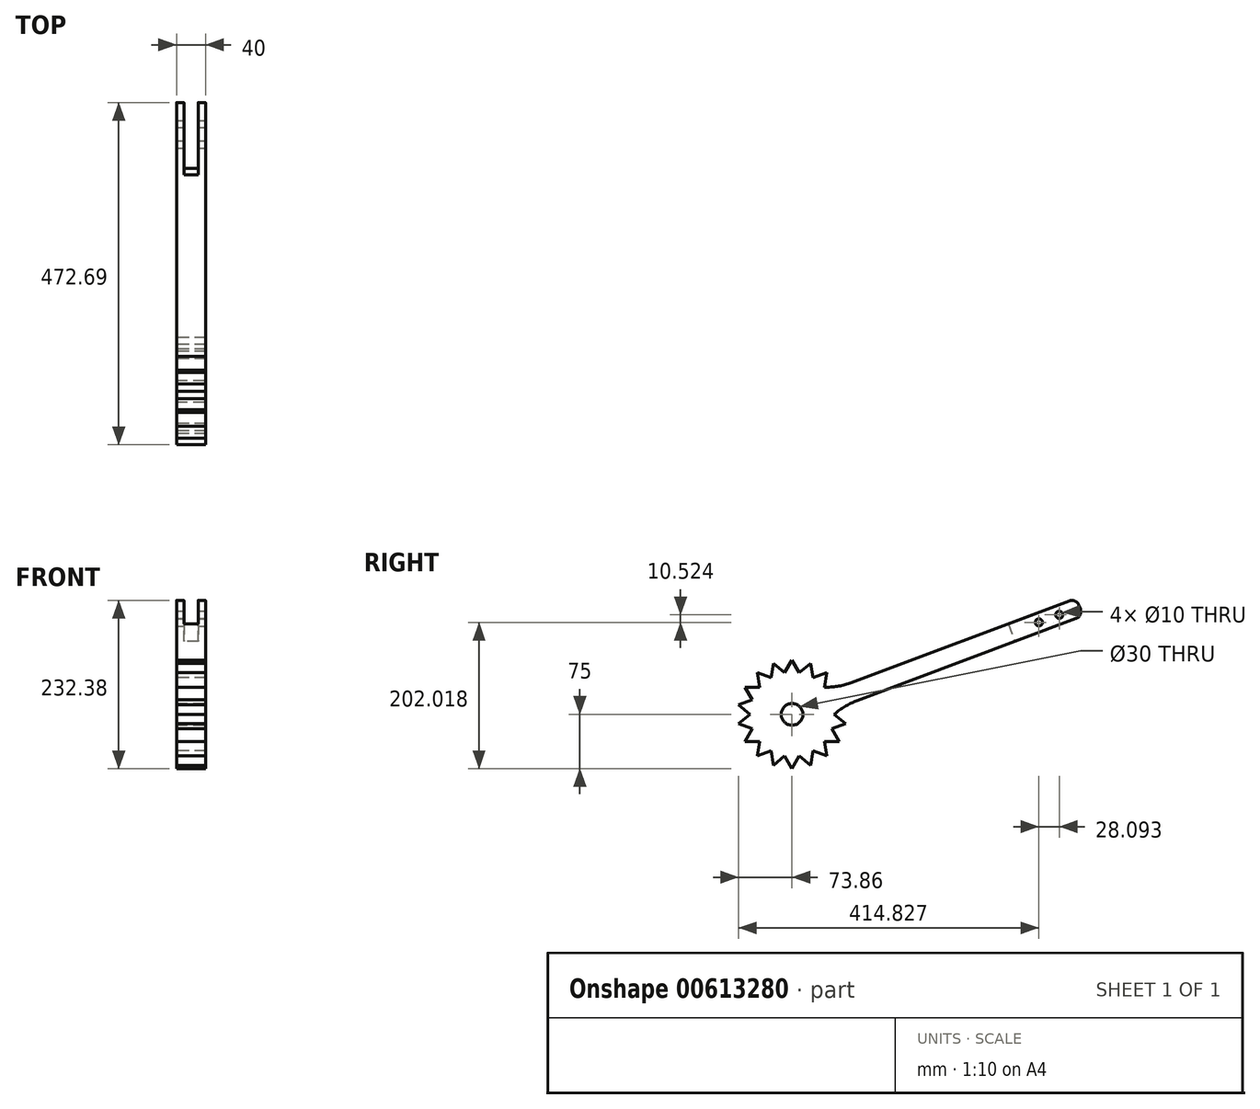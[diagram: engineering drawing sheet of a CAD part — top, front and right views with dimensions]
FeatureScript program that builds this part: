
annotation { "Feature Type Name" : "Feature", "Feature Type Description" : "" }
export const myFeature = defineFeature(function(context is Context, id is Id, definition is map)
    precondition{}
    {
        {
            var Q0;
            Q0=qCreatedBy(makeId("Right.planeOp"),FACE);
            var sketch = newSketch(context, id + "F0", { "sketchPlane" : qUnion([Q0])});
            skCircle(sketch, "E0", {"center": v(0, 0) * mm, "radius": 15 * mm});
            skCircle(sketch, "E1", {"center": v(0, 0) * mm, "radius": 37.5 * mm});
            skCircle(sketch, "E2.cCircle", {"center": v(0, 0) * mm, "radius": 37.5 * mm, "construction": true});
            skLineSegment(sketch, "E2.0", {"start": v(-64.95, 37.5) * mm, "end": v(64.95, 37.5) * mm});
            skLineSegment(sketch, "E2.1", {"start": v(64.95, 37.5) * mm, "end": v(0, -75) * mm});
            skLineSegment(sketch, "E2.2", {"start": v(0, -75) * mm, "end": v(-64.95, 37.5) * mm});
            skPoint(sketch, "E2.0.midPoint", {"position": v(0, 37.5) * mm});
            skLineSegment(sketch, "E3.0", {"start": v(-25.65, 70.48) * mm, "end": v(73.86, -13.02) * mm});
            skLineSegment(sketch, "E3.1", {"start": v(73.86, -13.02) * mm, "end": v(-48.2, -57.45) * mm});
            skLineSegment(sketch, "E3.2", {"start": v(-48.2, -57.45) * mm, "end": v(-25.65, 70.48) * mm});
            skPoint(sketch, "E3.0.midPoint", {"position": v(24.1, 28.73) * mm});
            skLineSegment(sketch, "E4.0", {"start": v(48.2, -57.45) * mm, "end": v(-73.86, -13.02) * mm});
            skLineSegment(sketch, "E4.1", {"start": v(-73.86, -13.02) * mm, "end": v(25.65, 70.48) * mm});
            skLineSegment(sketch, "E4.2", {"start": v(25.65, 70.48) * mm, "end": v(48.2, -57.45) * mm});
            skPoint(sketch, "E4.0.midPoint", {"position": v(-12.83, -35.24) * mm});
            skLineSegment(sketch, "E5.0", {"start": v(64.95, -37.5) * mm, "end": v(-64.95, -37.5) * mm});
            skLineSegment(sketch, "E5.1", {"start": v(-64.95, -37.5) * mm, "end": v(0, 75) * mm});
            skLineSegment(sketch, "E5.2", {"start": v(0, 75) * mm, "end": v(64.95, -37.5) * mm});
            skPoint(sketch, "E5.0.midPoint", {"position": v(0, -37.5) * mm});
            skLineSegment(sketch, "E6.0", {"start": v(25.65, -70.48) * mm, "end": v(-73.86, 13.02) * mm});
            skLineSegment(sketch, "E6.1", {"start": v(-73.86, 13.02) * mm, "end": v(48.2, 57.45) * mm});
            skLineSegment(sketch, "E6.2", {"start": v(48.2, 57.45) * mm, "end": v(25.65, -70.48) * mm});
            skPoint(sketch, "E6.0.midPoint", {"position": v(-24.1, -28.73) * mm});
            skLineSegment(sketch, "E7.0", {"start": v(73.86, 13.02) * mm, "end": v(-25.65, -70.48) * mm});
            skLineSegment(sketch, "E7.1", {"start": v(-25.65, -70.48) * mm, "end": v(-48.2, 57.45) * mm});
            skLineSegment(sketch, "E7.2", {"start": v(-48.2, 57.45) * mm, "end": v(73.86, 13.02) * mm});
            skPoint(sketch, "E7.0.midPoint", {"position": v(24.1, -28.73) * mm});
            skSolve(sketch);
        }
        {
            var Q0;
            {var subQ0=sQuery(id+"F0.wireOp",EDGE,"E2.2");var subQ1=sQuery(id+"F0.wireOp",EDGE,"E2.0");var subQ2=makeQuery(id+"F0.imprint","INTERSECT",VERTEX,{"derivedFrom":[subQ1,subQ0]});Q0=makeQuery(id+"F0.imprint","IMPRINT",FACE,{"disambiguationData":[TD([[makeQuery(id+"F0.imprint","IMPRINT",EDGE,{"disambiguationData":[TD([[subQ2,-1.0]])],"derivedFrom":subQ1}),-1.0]])]});}
            var Q1;
            {var subQ0=sQuery(id+"F0.wireOp",EDGE,"E7.1");var subQ1=sQuery(id+"F0.wireOp",EDGE,"E2.0");var subQ2=makeQuery(id+"F0.imprint","INTERSECT",VERTEX,{"derivedFrom":[subQ1,subQ0]});Q1=makeQuery(id+"F0.imprint","IMPRINT",FACE,{"disambiguationData":[TD([[makeQuery(id+"F0.imprint","IMPRINT",EDGE,{"disambiguationData":[TD([[subQ2,-1.0]])],"derivedFrom":subQ1}),1.0]])]});}
            var Q2;
            {var subQ0=sQuery(id+"F0.wireOp",EDGE,"E6.2");var subQ1=sQuery(id+"F0.wireOp",EDGE,"E2.0");var subQ2=makeQuery(id+"F0.imprint","INTERSECT",VERTEX,{"derivedFrom":[subQ1,subQ0]});Q2=makeQuery(id+"F0.imprint","IMPRINT",FACE,{"disambiguationData":[TD([[makeQuery(id+"F0.imprint","IMPRINT",EDGE,{"disambiguationData":[TD([[subQ2,1.0]])],"derivedFrom":subQ1}),1.0]])]});}
            var Q3;
            {var subQ0=sQuery(id+"F0.wireOp",EDGE,"E2.1");var subQ1=sQuery(id+"F0.wireOp",EDGE,"E2.0");var subQ2=makeQuery(id+"F0.imprint","INTERSECT",VERTEX,{"derivedFrom":[subQ1,subQ0]});Q3=makeQuery(id+"F0.imprint","IMPRINT",FACE,{"disambiguationData":[TD([[makeQuery(id+"F0.imprint","IMPRINT",EDGE,{"disambiguationData":[TD([[subQ2,1.0]])],"derivedFrom":subQ1}),-1.0]])]});}
            var Q4;
            {var subQ0=sQuery(id+"F0.wireOp",EDGE,"E7.2");var subQ1=sQuery(id+"F0.wireOp",EDGE,"E2.1");var subQ2=makeQuery(id+"F0.imprint","INTERSECT",VERTEX,{"derivedFrom":[subQ1,subQ0]});Q4=makeQuery(id+"F0.imprint","IMPRINT",FACE,{"disambiguationData":[TD([[makeQuery(id+"F0.imprint","IMPRINT",EDGE,{"disambiguationData":[TD([[subQ2,-1.0]])],"derivedFrom":subQ1}),1.0]])]});}
            var Q5;
            {var subQ0=sQuery(id+"F0.wireOp",EDGE,"E6.0");var subQ1=sQuery(id+"F0.wireOp",EDGE,"E2.1");var subQ2=makeQuery(id+"F0.imprint","INTERSECT",VERTEX,{"derivedFrom":[subQ1,subQ0]});Q5=makeQuery(id+"F0.imprint","IMPRINT",FACE,{"disambiguationData":[TD([[makeQuery(id+"F0.imprint","IMPRINT",EDGE,{"disambiguationData":[TD([[subQ2,1.0]])],"derivedFrom":subQ1}),1.0]])]});}
            var Q6;
            {var subQ0=sQuery(id+"F0.wireOp",EDGE,"E2.2");var subQ1=sQuery(id+"F0.wireOp",EDGE,"E2.1");var subQ2=makeQuery(id+"F0.imprint","INTERSECT",VERTEX,{"derivedFrom":[subQ1,subQ0]});Q6=makeQuery(id+"F0.imprint","IMPRINT",FACE,{"disambiguationData":[TD([[makeQuery(id+"F0.imprint","IMPRINT",EDGE,{"disambiguationData":[TD([[subQ2,1.0]])],"derivedFrom":subQ1}),-1.0]])]});}
            var Q7;
            {var subQ0=sQuery(id+"F0.wireOp",EDGE,"E7.0");var subQ1=sQuery(id+"F0.wireOp",EDGE,"E2.2");var subQ2=makeQuery(id+"F0.imprint","INTERSECT",VERTEX,{"derivedFrom":[subQ1,subQ0]});Q7=makeQuery(id+"F0.imprint","IMPRINT",FACE,{"disambiguationData":[TD([[makeQuery(id+"F0.imprint","IMPRINT",EDGE,{"disambiguationData":[TD([[subQ2,-1.0]])],"derivedFrom":subQ1}),1.0]])]});}
            var Q8;
            {var subQ0=sQuery(id+"F0.wireOp",EDGE,"E6.1");var subQ1=sQuery(id+"F0.wireOp",EDGE,"E2.2");var subQ2=makeQuery(id+"F0.imprint","INTERSECT",VERTEX,{"derivedFrom":[subQ1,subQ0]});Q8=makeQuery(id+"F0.imprint","IMPRINT",FACE,{"disambiguationData":[TD([[makeQuery(id+"F0.imprint","IMPRINT",EDGE,{"disambiguationData":[TD([[subQ2,1.0]])],"derivedFrom":subQ1}),1.0]])]});}
            var Q9;
            {var subQ0=sQuery(id+"F0.wireOp",EDGE,"E3.2");var subQ1=sQuery(id+"F0.wireOp",EDGE,"E3.0");var subQ2=makeQuery(id+"F0.imprint","INTERSECT",VERTEX,{"derivedFrom":[subQ1,subQ0]});Q9=makeQuery(id+"F0.imprint","IMPRINT",FACE,{"disambiguationData":[TD([[makeQuery(id+"F0.imprint","IMPRINT",EDGE,{"disambiguationData":[TD([[subQ2,-1.0]])],"derivedFrom":subQ1}),-1.0]])]});}
            var Q10;
            {var subQ0=sQuery(id+"F0.wireOp",EDGE,"E5.1");var subQ1=sQuery(id+"F0.wireOp",EDGE,"E3.0");var subQ2=makeQuery(id+"F0.imprint","INTERSECT",VERTEX,{"derivedFrom":[subQ1,subQ0]});Q10=makeQuery(id+"F0.imprint","IMPRINT",FACE,{"disambiguationData":[TD([[makeQuery(id+"F0.imprint","IMPRINT",EDGE,{"disambiguationData":[TD([[subQ2,-1.0]])],"derivedFrom":subQ1}),1.0]])]});}
            var Q11;
            {var subQ0=sQuery(id+"F0.wireOp",EDGE,"E3.1");var subQ1=sQuery(id+"F0.wireOp",EDGE,"E3.0");var subQ2=makeQuery(id+"F0.imprint","INTERSECT",VERTEX,{"derivedFrom":[subQ1,subQ0]});Q11=makeQuery(id+"F0.imprint","IMPRINT",FACE,{"disambiguationData":[TD([[makeQuery(id+"F0.imprint","IMPRINT",EDGE,{"disambiguationData":[TD([[subQ2,1.0]])],"derivedFrom":subQ1}),-1.0]])]});}
            var Q12;
            {var subQ0=sQuery(id+"F0.wireOp",EDGE,"E5.2");var subQ1=sQuery(id+"F0.wireOp",EDGE,"E3.1");var subQ2=makeQuery(id+"F0.imprint","INTERSECT",VERTEX,{"derivedFrom":[subQ1,subQ0]});Q12=makeQuery(id+"F0.imprint","IMPRINT",FACE,{"disambiguationData":[TD([[makeQuery(id+"F0.imprint","IMPRINT",EDGE,{"disambiguationData":[TD([[subQ2,-1.0]])],"derivedFrom":subQ1}),1.0]])]});}
            var Q13;
            {var subQ0=sQuery(id+"F0.wireOp",EDGE,"E3.2");var subQ1=sQuery(id+"F0.wireOp",EDGE,"E3.1");var subQ2=makeQuery(id+"F0.imprint","INTERSECT",VERTEX,{"derivedFrom":[subQ1,subQ0]});Q13=makeQuery(id+"F0.imprint","IMPRINT",FACE,{"disambiguationData":[TD([[makeQuery(id+"F0.imprint","IMPRINT",EDGE,{"disambiguationData":[TD([[subQ2,1.0]])],"derivedFrom":subQ1}),-1.0]])]});}
            var Q14;
            {var subQ0=sQuery(id+"F0.wireOp",EDGE,"E5.0");var subQ1=sQuery(id+"F0.wireOp",EDGE,"E3.2");var subQ2=makeQuery(id+"F0.imprint","INTERSECT",VERTEX,{"derivedFrom":[subQ1,subQ0]});Q14=makeQuery(id+"F0.imprint","IMPRINT",FACE,{"disambiguationData":[TD([[makeQuery(id+"F0.imprint","IMPRINT",EDGE,{"disambiguationData":[TD([[subQ2,-1.0]])],"derivedFrom":subQ1}),1.0]])]});}
            var Q15;
            {var subQ0=sQuery(id+"F0.wireOp",EDGE,"E4.2");var subQ1=sQuery(id+"F0.wireOp",EDGE,"E4.0");var subQ2=makeQuery(id+"F0.imprint","INTERSECT",VERTEX,{"derivedFrom":[subQ1,subQ0]});Q15=makeQuery(id+"F0.imprint","IMPRINT",FACE,{"disambiguationData":[TD([[makeQuery(id+"F0.imprint","IMPRINT",EDGE,{"disambiguationData":[TD([[subQ2,-1.0]])],"derivedFrom":subQ1}),-1.0]])]});}
            var Q16;
            {var subQ0=sQuery(id+"F0.wireOp",EDGE,"E4.1");var subQ1=sQuery(id+"F0.wireOp",EDGE,"E4.0");var subQ2=makeQuery(id+"F0.imprint","INTERSECT",VERTEX,{"derivedFrom":[subQ1,subQ0]});Q16=makeQuery(id+"F0.imprint","IMPRINT",FACE,{"disambiguationData":[TD([[makeQuery(id+"F0.imprint","IMPRINT",EDGE,{"disambiguationData":[TD([[subQ2,1.0]])],"derivedFrom":subQ1}),-1.0]])]});}
            var Q17;
            {var subQ0=sQuery(id+"F0.wireOp",EDGE,"E4.2");var subQ1=sQuery(id+"F0.wireOp",EDGE,"E4.1");var subQ2=makeQuery(id+"F0.imprint","INTERSECT",VERTEX,{"derivedFrom":[subQ1,subQ0]});Q17=makeQuery(id+"F0.imprint","IMPRINT",FACE,{"disambiguationData":[TD([[makeQuery(id+"F0.imprint","IMPRINT",EDGE,{"disambiguationData":[TD([[subQ2,1.0]])],"derivedFrom":subQ1}),-1.0]])]});}
            var Q18;
            {var subQ0=sQuery(id+"F0.wireOp",EDGE,"E7.1");var subQ1=sQuery(id+"F0.wireOp",EDGE,"E2.0");var subQ2=makeQuery(id+"F0.imprint","INTERSECT",VERTEX,{"derivedFrom":[subQ1,subQ0]});Q18=makeQuery(id+"F0.imprint","IMPRINT",FACE,{"disambiguationData":[TD([[makeQuery(id+"F0.imprint","IMPRINT",EDGE,{"disambiguationData":[TD([[subQ2,-1.0]])],"derivedFrom":subQ1}),-1.0]])]});}
            var Q19;
            {var subQ0=sQuery(id+"F0.wireOp",EDGE,"E3.2");var subQ1=sQuery(id+"F0.wireOp",EDGE,"E2.0");var subQ2=makeQuery(id+"F0.imprint","INTERSECT",VERTEX,{"derivedFrom":[subQ1,subQ0]});Q19=makeQuery(id+"F0.imprint","IMPRINT",FACE,{"disambiguationData":[TD([[makeQuery(id+"F0.imprint","IMPRINT",EDGE,{"disambiguationData":[TD([[subQ2,-1.0]])],"derivedFrom":subQ1}),1.0]])]});}
            var Q20;
            {var subQ0=sQuery(id+"F0.wireOp",EDGE,"E5.2");var subQ1=sQuery(id+"F0.wireOp",EDGE,"E2.0");var subQ2=makeQuery(id+"F0.imprint","INTERSECT",VERTEX,{"derivedFrom":[subQ1,subQ0]});Q20=makeQuery(id+"F0.imprint","IMPRINT",FACE,{"disambiguationData":[TD([[makeQuery(id+"F0.imprint","IMPRINT",EDGE,{"disambiguationData":[TD([[subQ2,-1.0]])],"derivedFrom":subQ1}),1.0]])]});}
            var Q21;
            {var subQ0=sQuery(id+"F0.wireOp",EDGE,"E6.2");var subQ1=sQuery(id+"F0.wireOp",EDGE,"E2.0");var subQ2=makeQuery(id+"F0.imprint","INTERSECT",VERTEX,{"derivedFrom":[subQ1,subQ0]});Q21=makeQuery(id+"F0.imprint","IMPRINT",FACE,{"disambiguationData":[TD([[makeQuery(id+"F0.imprint","IMPRINT",EDGE,{"disambiguationData":[TD([[subQ2,1.0]])],"derivedFrom":subQ1}),-1.0]])]});}
            var Q22;
            {var subQ0=sQuery(id+"F0.wireOp",EDGE,"E7.2");var subQ1=sQuery(id+"F0.wireOp",EDGE,"E2.1");var subQ2=makeQuery(id+"F0.imprint","INTERSECT",VERTEX,{"derivedFrom":[subQ1,subQ0]});Q22=makeQuery(id+"F0.imprint","IMPRINT",FACE,{"disambiguationData":[TD([[makeQuery(id+"F0.imprint","IMPRINT",EDGE,{"disambiguationData":[TD([[subQ2,-1.0]])],"derivedFrom":subQ1}),-1.0]])]});}
            var Q23;
            {var subQ0=sQuery(id+"F0.wireOp",EDGE,"E3.0");var subQ1=sQuery(id+"F0.wireOp",EDGE,"E2.1");var subQ2=makeQuery(id+"F0.imprint","INTERSECT",VERTEX,{"derivedFrom":[subQ1,subQ0]});Q23=makeQuery(id+"F0.imprint","IMPRINT",FACE,{"disambiguationData":[TD([[makeQuery(id+"F0.imprint","IMPRINT",EDGE,{"disambiguationData":[TD([[subQ2,-1.0]])],"derivedFrom":subQ1}),1.0]])]});}
            var Q24;
            {var subQ0=sQuery(id+"F0.wireOp",EDGE,"E5.0");var subQ1=sQuery(id+"F0.wireOp",EDGE,"E2.1");var subQ2=makeQuery(id+"F0.imprint","INTERSECT",VERTEX,{"derivedFrom":[subQ1,subQ0]});Q24=makeQuery(id+"F0.imprint","IMPRINT",FACE,{"disambiguationData":[TD([[makeQuery(id+"F0.imprint","IMPRINT",EDGE,{"disambiguationData":[TD([[subQ2,-1.0]])],"derivedFrom":subQ1}),1.0]])]});}
            var Q25;
            {var subQ0=sQuery(id+"F0.wireOp",EDGE,"E6.0");var subQ1=sQuery(id+"F0.wireOp",EDGE,"E2.1");var subQ2=makeQuery(id+"F0.imprint","INTERSECT",VERTEX,{"derivedFrom":[subQ1,subQ0]});Q25=makeQuery(id+"F0.imprint","IMPRINT",FACE,{"disambiguationData":[TD([[makeQuery(id+"F0.imprint","IMPRINT",EDGE,{"disambiguationData":[TD([[subQ2,1.0]])],"derivedFrom":subQ1}),-1.0]])]});}
            var Q26;
            {var subQ0=sQuery(id+"F0.wireOp",EDGE,"E7.0");var subQ1=sQuery(id+"F0.wireOp",EDGE,"E2.2");var subQ2=makeQuery(id+"F0.imprint","INTERSECT",VERTEX,{"derivedFrom":[subQ1,subQ0]});Q26=makeQuery(id+"F0.imprint","IMPRINT",FACE,{"disambiguationData":[TD([[makeQuery(id+"F0.imprint","IMPRINT",EDGE,{"disambiguationData":[TD([[subQ2,-1.0]])],"derivedFrom":subQ1}),-1.0]])]});}
            var Q27;
            {var subQ0=sQuery(id+"F0.wireOp",EDGE,"E3.1");var subQ1=sQuery(id+"F0.wireOp",EDGE,"E2.2");var subQ2=makeQuery(id+"F0.imprint","INTERSECT",VERTEX,{"derivedFrom":[subQ1,subQ0]});Q27=makeQuery(id+"F0.imprint","IMPRINT",FACE,{"disambiguationData":[TD([[makeQuery(id+"F0.imprint","IMPRINT",EDGE,{"disambiguationData":[TD([[subQ2,-1.0]])],"derivedFrom":subQ1}),1.0]])]});}
            var Q28;
            {var subQ0=sQuery(id+"F0.wireOp",EDGE,"E5.1");var subQ1=sQuery(id+"F0.wireOp",EDGE,"E2.2");var subQ2=makeQuery(id+"F0.imprint","INTERSECT",VERTEX,{"derivedFrom":[subQ1,subQ0]});Q28=makeQuery(id+"F0.imprint","IMPRINT",FACE,{"disambiguationData":[TD([[makeQuery(id+"F0.imprint","IMPRINT",EDGE,{"disambiguationData":[TD([[subQ2,-1.0]])],"derivedFrom":subQ1}),1.0]])]});}
            var Q29;
            {var subQ0=sQuery(id+"F0.wireOp",EDGE,"E6.1");var subQ1=sQuery(id+"F0.wireOp",EDGE,"E2.2");var subQ2=makeQuery(id+"F0.imprint","INTERSECT",VERTEX,{"derivedFrom":[subQ1,subQ0]});Q29=makeQuery(id+"F0.imprint","IMPRINT",FACE,{"disambiguationData":[TD([[makeQuery(id+"F0.imprint","IMPRINT",EDGE,{"disambiguationData":[TD([[subQ2,1.0]])],"derivedFrom":subQ1}),-1.0]])]});}
            var Q30;
            {var subQ0=sQuery(id+"F0.wireOp",EDGE,"E5.1");var subQ1=sQuery(id+"F0.wireOp",EDGE,"E3.0");var subQ2=makeQuery(id+"F0.imprint","INTERSECT",VERTEX,{"derivedFrom":[subQ1,subQ0]});Q30=makeQuery(id+"F0.imprint","IMPRINT",FACE,{"disambiguationData":[TD([[makeQuery(id+"F0.imprint","IMPRINT",EDGE,{"disambiguationData":[TD([[subQ2,-1.0]])],"derivedFrom":subQ1}),-1.0]])]});}
            var Q31;
            {var subQ0=sQuery(id+"F0.wireOp",EDGE,"E4.1");var subQ1=sQuery(id+"F0.wireOp",EDGE,"E3.0");var subQ2=makeQuery(id+"F0.imprint","INTERSECT",VERTEX,{"derivedFrom":[subQ1,subQ0]});Q31=makeQuery(id+"F0.imprint","IMPRINT",FACE,{"disambiguationData":[TD([[makeQuery(id+"F0.imprint","IMPRINT",EDGE,{"disambiguationData":[TD([[subQ2,-1.0]])],"derivedFrom":subQ1}),1.0]])]});}
            var Q32;
            {var subQ0=sQuery(id+"F0.wireOp",EDGE,"E5.2");var subQ1=sQuery(id+"F0.wireOp",EDGE,"E3.1");var subQ2=makeQuery(id+"F0.imprint","INTERSECT",VERTEX,{"derivedFrom":[subQ1,subQ0]});Q32=makeQuery(id+"F0.imprint","IMPRINT",FACE,{"disambiguationData":[TD([[makeQuery(id+"F0.imprint","IMPRINT",EDGE,{"disambiguationData":[TD([[subQ2,-1.0]])],"derivedFrom":subQ1}),-1.0]])]});}
            var Q33;
            {var subQ0=sQuery(id+"F0.wireOp",EDGE,"E4.2");var subQ1=sQuery(id+"F0.wireOp",EDGE,"E3.1");var subQ2=makeQuery(id+"F0.imprint","INTERSECT",VERTEX,{"derivedFrom":[subQ1,subQ0]});Q33=makeQuery(id+"F0.imprint","IMPRINT",FACE,{"disambiguationData":[TD([[makeQuery(id+"F0.imprint","IMPRINT",EDGE,{"disambiguationData":[TD([[subQ2,-1.0]])],"derivedFrom":subQ1}),1.0]])]});}
            var Q34;
            {var subQ0=sQuery(id+"F0.wireOp",EDGE,"E5.0");var subQ1=sQuery(id+"F0.wireOp",EDGE,"E3.2");var subQ2=makeQuery(id+"F0.imprint","INTERSECT",VERTEX,{"derivedFrom":[subQ1,subQ0]});Q34=makeQuery(id+"F0.imprint","IMPRINT",FACE,{"disambiguationData":[TD([[makeQuery(id+"F0.imprint","IMPRINT",EDGE,{"disambiguationData":[TD([[subQ2,-1.0]])],"derivedFrom":subQ1}),-1.0]])]});}
            var Q35;
            {var subQ0=sQuery(id+"F0.wireOp",EDGE,"E4.0");var subQ1=sQuery(id+"F0.wireOp",EDGE,"E3.2");var subQ2=makeQuery(id+"F0.imprint","INTERSECT",VERTEX,{"derivedFrom":[subQ1,subQ0]});Q35=makeQuery(id+"F0.imprint","IMPRINT",FACE,{"disambiguationData":[TD([[makeQuery(id+"F0.imprint","IMPRINT",EDGE,{"disambiguationData":[TD([[subQ2,-1.0]])],"derivedFrom":subQ1}),1.0]])]});}
            var Q36;
            {var subQ0=sQuery(id+"F0.wireOp",EDGE,"E7.2");var subQ1=sQuery(id+"F0.wireOp",EDGE,"E2.0");var subQ2=makeQuery(id+"F0.imprint","INTERSECT",VERTEX,{"derivedFrom":[subQ1,subQ0]});Q36=makeQuery(id+"F0.imprint","IMPRINT",FACE,{"disambiguationData":[TD([[makeQuery(id+"F0.imprint","IMPRINT",EDGE,{"disambiguationData":[TD([[subQ2,-1.0]])],"derivedFrom":subQ1}),1.0]])]});}
            var Q37;
            {var subQ0=sQuery(id+"F0.wireOp",EDGE,"E4.2");var subQ1=sQuery(id+"F0.wireOp",EDGE,"E3.0");var subQ2=makeQuery(id+"F0.imprint","INTERSECT",VERTEX,{"derivedFrom":[subQ1,subQ0]});Q37=makeQuery(id+"F0.imprint","IMPRINT",FACE,{"disambiguationData":[TD([[makeQuery(id+"F0.imprint","IMPRINT",EDGE,{"disambiguationData":[TD([[subQ2,-1.0]])],"derivedFrom":subQ1}),-1.0]])]});}
            var Q38;
            {var subQ0=sQuery(id+"F0.wireOp",EDGE,"E2.1");var subQ1=makeQuery(id+"F0.imprint","INTERSECT",VERTEX,{"derivedFrom":[sQuery(id+"F0.wireOp",EDGE,"E1"),subQ0]});Q38=makeQuery(id+"F0.imprint","IMPRINT",FACE,{"disambiguationData":[TD([[makeQuery(id+"F0.imprint","IMPRINT",EDGE,{"disambiguationData":[TD([[subQ1,1.0]])],"derivedFrom":subQ0}),1.0]])]});}
            var Q39;
            {var subQ0=sQuery(id+"F0.wireOp",EDGE,"E7.0");var subQ1=sQuery(id+"F0.wireOp",EDGE,"E2.1");var subQ2=makeQuery(id+"F0.imprint","INTERSECT",VERTEX,{"derivedFrom":[subQ1,subQ0]});Q39=makeQuery(id+"F0.imprint","IMPRINT",FACE,{"disambiguationData":[TD([[makeQuery(id+"F0.imprint","IMPRINT",EDGE,{"disambiguationData":[TD([[subQ2,-1.0]])],"derivedFrom":subQ1}),-1.0]])]});}
            var Q40;
            {var subQ0=sQuery(id+"F0.wireOp",EDGE,"E2.2");var subQ1=makeQuery(id+"F0.imprint","INTERSECT",VERTEX,{"derivedFrom":[sQuery(id+"F0.wireOp",EDGE,"E1"),subQ0]});Q40=makeQuery(id+"F0.imprint","IMPRINT",FACE,{"disambiguationData":[TD([[makeQuery(id+"F0.imprint","IMPRINT",EDGE,{"disambiguationData":[TD([[subQ1,1.0]])],"derivedFrom":subQ0}),1.0]])]});}
            var Q41;
            {var subQ0=sQuery(id+"F0.wireOp",EDGE,"E4.0");var subQ1=makeQuery(id+"F0.imprint","INTERSECT",VERTEX,{"derivedFrom":[sQuery(id+"F0.wireOp",EDGE,"E1"),subQ0]});Q41=makeQuery(id+"F0.imprint","IMPRINT",FACE,{"disambiguationData":[TD([[makeQuery(id+"F0.imprint","IMPRINT",EDGE,{"disambiguationData":[TD([[subQ1,1.0]])],"derivedFrom":subQ0}),1.0]])]});}
            var Q42;
            Q42=makeQuery(id+"F0.imprint","IMPRINT",FACE,{"disambiguationData":[TD([[makeQuery(id+"F0.imprint","IMPRINT",EDGE,{"derivedFrom":sQuery(id+"F0.wireOp",EDGE,"E0")}),1.0]])]});
            var Q43;
            {var subQ0=sQuery(id+"F0.wireOp",EDGE,"E4.1");var subQ1=sQuery(id+"F0.wireOp",EDGE,"E3.2");var subQ2=makeQuery(id+"F0.imprint","INTERSECT",VERTEX,{"derivedFrom":[subQ1,subQ0]});Q43=makeQuery(id+"F0.imprint","IMPRINT",FACE,{"disambiguationData":[TD([[makeQuery(id+"F0.imprint","IMPRINT",EDGE,{"disambiguationData":[TD([[subQ2,-1.0]])],"derivedFrom":subQ1}),1.0]])]});}
            var Q44;
            {var subQ0=sQuery(id+"F0.wireOp",EDGE,"E4.0");var subQ1=sQuery(id+"F0.wireOp",EDGE,"E3.1");var subQ2=makeQuery(id+"F0.imprint","INTERSECT",VERTEX,{"derivedFrom":[subQ1,subQ0]});Q44=makeQuery(id+"F0.imprint","IMPRINT",FACE,{"disambiguationData":[TD([[makeQuery(id+"F0.imprint","IMPRINT",EDGE,{"disambiguationData":[TD([[subQ2,-1.0]])],"derivedFrom":subQ1}),-1.0]])]});}
            var Q45;
            {var subQ0=sQuery(id+"F0.wireOp",EDGE,"E4.2");var subQ1=sQuery(id+"F0.wireOp",EDGE,"E2.1");var subQ2=makeQuery(id+"F0.imprint","INTERSECT",VERTEX,{"derivedFrom":[subQ1,subQ0]});Q45=makeQuery(id+"F0.imprint","IMPRINT",FACE,{"disambiguationData":[TD([[makeQuery(id+"F0.imprint","IMPRINT",EDGE,{"disambiguationData":[TD([[subQ2,-1.0]])],"derivedFrom":subQ1}),1.0]])]});}
            var Q46;
            {var subQ0=sQuery(id+"F0.wireOp",EDGE,"E3.2");var subQ1=sQuery(id+"F0.wireOp",EDGE,"E2.2");var subQ2=makeQuery(id+"F0.imprint","INTERSECT",VERTEX,{"derivedFrom":[subQ1,subQ0]});Q46=makeQuery(id+"F0.imprint","IMPRINT",FACE,{"disambiguationData":[TD([[makeQuery(id+"F0.imprint","IMPRINT",EDGE,{"disambiguationData":[TD([[subQ2,-1.0]])],"derivedFrom":subQ1}),-1.0]])]});}
            var Q47;
            {var subQ0=sQuery(id+"F0.wireOp",EDGE,"E5.1");var subQ1=sQuery(id+"F0.wireOp",EDGE,"E3.2");var subQ2=makeQuery(id+"F0.imprint","INTERSECT",VERTEX,{"derivedFrom":[subQ1,subQ0]});Q47=makeQuery(id+"F0.imprint","IMPRINT",FACE,{"disambiguationData":[TD([[makeQuery(id+"F0.imprint","IMPRINT",EDGE,{"disambiguationData":[TD([[subQ2,-1.0]])],"derivedFrom":subQ1}),-1.0]])]});}
            var Q48;
            {var subQ0=sQuery(id+"F0.wireOp",EDGE,"E7.1");var subQ1=sQuery(id+"F0.wireOp",EDGE,"E2.2");var subQ2=makeQuery(id+"F0.imprint","INTERSECT",VERTEX,{"derivedFrom":[subQ1,subQ0]});Q48=makeQuery(id+"F0.imprint","IMPRINT",FACE,{"disambiguationData":[TD([[makeQuery(id+"F0.imprint","IMPRINT",EDGE,{"disambiguationData":[TD([[subQ2,-1.0]])],"derivedFrom":subQ1}),1.0]])]});}
            var Q49;
            {var subQ0=sQuery(id+"F0.wireOp",EDGE,"E5.0");var subQ1=sQuery(id+"F0.wireOp",EDGE,"E2.2");var subQ2=makeQuery(id+"F0.imprint","INTERSECT",VERTEX,{"derivedFrom":[subQ1,subQ0]});Q49=makeQuery(id+"F0.imprint","IMPRINT",FACE,{"disambiguationData":[TD([[makeQuery(id+"F0.imprint","IMPRINT",EDGE,{"disambiguationData":[TD([[subQ2,-1.0]])],"derivedFrom":subQ1}),-1.0]])]});}
            var Q50;
            {var subQ0=sQuery(id+"F0.wireOp",EDGE,"E7.0");var subQ1=sQuery(id+"F0.wireOp",EDGE,"E2.1");var subQ2=makeQuery(id+"F0.imprint","INTERSECT",VERTEX,{"derivedFrom":[subQ1,subQ0]});Q50=makeQuery(id+"F0.imprint","IMPRINT",FACE,{"disambiguationData":[TD([[makeQuery(id+"F0.imprint","IMPRINT",EDGE,{"disambiguationData":[TD([[subQ2,-1.0]])],"derivedFrom":subQ1}),1.0]])]});}
            var Q51;
            Q51=makeQuery(id+"F0.imprint","IMPRINT",FACE,{"disambiguationData":[TD([[makeQuery(id+"F0.imprint","IMPRINT",EDGE,{"derivedFrom":sQuery(id+"F0.wireOp",EDGE,"E0")}),-1.0]])]});
            var Q52;
            {var subQ0=sQuery(id+"F0.wireOp",EDGE,"E4.1");var subQ1=sQuery(id+"F0.wireOp",EDGE,"E3.2");var subQ2=makeQuery(id+"F0.imprint","INTERSECT",VERTEX,{"derivedFrom":[subQ1,subQ0]});Q52=makeQuery(id+"F0.imprint","IMPRINT",FACE,{"disambiguationData":[TD([[makeQuery(id+"F0.imprint","IMPRINT",EDGE,{"disambiguationData":[TD([[subQ2,-1.0]])],"derivedFrom":subQ1}),-1.0]])]});}
            var Q53;
            {var subQ0=sQuery(id+"F0.wireOp",EDGE,"E4.2");var subQ1=sQuery(id+"F0.wireOp",EDGE,"E2.1");var subQ2=makeQuery(id+"F0.imprint","INTERSECT",VERTEX,{"derivedFrom":[subQ1,subQ0]});Q53=makeQuery(id+"F0.imprint","IMPRINT",FACE,{"disambiguationData":[TD([[makeQuery(id+"F0.imprint","IMPRINT",EDGE,{"disambiguationData":[TD([[subQ2,-1.0]])],"derivedFrom":subQ1}),-1.0]])]});}
            var Q54;
            {var subQ0=sQuery(id+"F0.wireOp",EDGE,"E5.1");var subQ1=sQuery(id+"F0.wireOp",EDGE,"E2.0");var subQ2=makeQuery(id+"F0.imprint","INTERSECT",VERTEX,{"derivedFrom":[subQ1,subQ0]});Q54=makeQuery(id+"F0.imprint","IMPRINT",FACE,{"disambiguationData":[TD([[makeQuery(id+"F0.imprint","IMPRINT",EDGE,{"disambiguationData":[TD([[subQ2,-1.0]])],"derivedFrom":subQ1}),-1.0]])]});}
            var Q55;
            {var subQ0=sQuery(id+"F0.wireOp",EDGE,"E5.2");var subQ1=sQuery(id+"F0.wireOp",EDGE,"E3.0");var subQ2=makeQuery(id+"F0.imprint","INTERSECT",VERTEX,{"derivedFrom":[subQ1,subQ0]});Q55=makeQuery(id+"F0.imprint","IMPRINT",FACE,{"disambiguationData":[TD([[makeQuery(id+"F0.imprint","IMPRINT",EDGE,{"disambiguationData":[TD([[subQ2,-1.0]])],"derivedFrom":subQ1}),-1.0]])]});}
            var Q56;
            {var subQ0=sQuery(id+"F0.wireOp",EDGE,"E5.1");var subQ1=sQuery(id+"F0.wireOp",EDGE,"E3.2");var subQ2=makeQuery(id+"F0.imprint","INTERSECT",VERTEX,{"derivedFrom":[subQ1,subQ0]});Q56=makeQuery(id+"F0.imprint","IMPRINT",FACE,{"disambiguationData":[TD([[makeQuery(id+"F0.imprint","IMPRINT",EDGE,{"disambiguationData":[TD([[subQ2,-1.0]])],"derivedFrom":subQ1}),1.0]])]});}
            var Q57;
            {var subQ0=sQuery(id+"F0.wireOp",EDGE,"E3.1");var subQ1=sQuery(id+"F0.wireOp",EDGE,"E2.2");var subQ2=makeQuery(id+"F0.imprint","INTERSECT",VERTEX,{"derivedFrom":[subQ1,subQ0]});Q57=makeQuery(id+"F0.imprint","IMPRINT",FACE,{"disambiguationData":[TD([[makeQuery(id+"F0.imprint","IMPRINT",EDGE,{"disambiguationData":[TD([[subQ2,-1.0]])],"derivedFrom":subQ1}),-1.0]])]});}
            var Q58;
            {var subQ0=sQuery(id+"F0.wireOp",EDGE,"E5.2");var subQ1=sQuery(id+"F0.wireOp",EDGE,"E2.1");var subQ2=makeQuery(id+"F0.imprint","INTERSECT",VERTEX,{"derivedFrom":[subQ1,subQ0]});Q58=makeQuery(id+"F0.imprint","IMPRINT",FACE,{"disambiguationData":[TD([[makeQuery(id+"F0.imprint","IMPRINT",EDGE,{"disambiguationData":[TD([[subQ2,-1.0]])],"derivedFrom":subQ1}),1.0]])]});}
            var Q59;
            {var subQ0=sQuery(id+"F0.wireOp",EDGE,"E4.1");var subQ1=sQuery(id+"F0.wireOp",EDGE,"E2.0");var subQ2=makeQuery(id+"F0.imprint","INTERSECT",VERTEX,{"derivedFrom":[subQ1,subQ0]});Q59=makeQuery(id+"F0.imprint","IMPRINT",FACE,{"disambiguationData":[TD([[makeQuery(id+"F0.imprint","IMPRINT",EDGE,{"disambiguationData":[TD([[subQ2,-1.0]])],"derivedFrom":subQ1}),-1.0]])]});}
            var Q60;
            {var subQ0=sQuery(id+"F0.wireOp",EDGE,"E7.2");var subQ1=sQuery(id+"F0.wireOp",EDGE,"E2.0");var subQ2=makeQuery(id+"F0.imprint","INTERSECT",VERTEX,{"derivedFrom":[subQ1,subQ0]});Q60=makeQuery(id+"F0.imprint","IMPRINT",FACE,{"disambiguationData":[TD([[makeQuery(id+"F0.imprint","IMPRINT",EDGE,{"disambiguationData":[TD([[subQ2,-1.0]])],"derivedFrom":subQ1}),-1.0]])]});}
            var Q61;
            {var subQ0=sQuery(id+"F0.wireOp",EDGE,"E3.2");var subQ1=makeQuery(id+"F0.imprint","INTERSECT",VERTEX,{"derivedFrom":[sQuery(id+"F0.wireOp",EDGE,"E1"),subQ0]});Q61=makeQuery(id+"F0.imprint","IMPRINT",FACE,{"disambiguationData":[TD([[makeQuery(id+"F0.imprint","IMPRINT",EDGE,{"disambiguationData":[TD([[subQ1,1.0]])],"derivedFrom":subQ0}),1.0]])]});}
            var Q62;
            {var subQ0=sQuery(id+"F0.wireOp",EDGE,"E5.2");var subQ1=sQuery(id+"F0.wireOp",EDGE,"E3.0");var subQ2=makeQuery(id+"F0.imprint","INTERSECT",VERTEX,{"derivedFrom":[subQ1,subQ0]});Q62=makeQuery(id+"F0.imprint","IMPRINT",FACE,{"disambiguationData":[TD([[makeQuery(id+"F0.imprint","IMPRINT",EDGE,{"disambiguationData":[TD([[subQ2,-1.0]])],"derivedFrom":subQ1}),1.0]])]});}
            var Q63;
            {var subQ0=sQuery(id+"F0.wireOp",EDGE,"E3.2");var subQ1=sQuery(id+"F0.wireOp",EDGE,"E2.0");var subQ2=makeQuery(id+"F0.imprint","INTERSECT",VERTEX,{"derivedFrom":[subQ1,subQ0]});Q63=makeQuery(id+"F0.imprint","IMPRINT",FACE,{"disambiguationData":[TD([[makeQuery(id+"F0.imprint","IMPRINT",EDGE,{"disambiguationData":[TD([[subQ2,-1.0]])],"derivedFrom":subQ1}),-1.0]])]});}
            var Q64;
            {var subQ0=sQuery(id+"F0.wireOp",EDGE,"E4.0");var subQ1=sQuery(id+"F0.wireOp",EDGE,"E2.2");var subQ2=makeQuery(id+"F0.imprint","INTERSECT",VERTEX,{"derivedFrom":[subQ1,subQ0]});Q64=makeQuery(id+"F0.imprint","IMPRINT",FACE,{"disambiguationData":[TD([[makeQuery(id+"F0.imprint","IMPRINT",EDGE,{"disambiguationData":[TD([[subQ2,-1.0]])],"derivedFrom":subQ1}),1.0]])]});}
            var Q65;
            {var subQ0=sQuery(id+"F0.wireOp",EDGE,"E4.1");var subQ1=makeQuery(id+"F0.imprint","INTERSECT",VERTEX,{"derivedFrom":[sQuery(id+"F0.wireOp",EDGE,"E1"),subQ0]});Q65=makeQuery(id+"F0.imprint","IMPRINT",FACE,{"disambiguationData":[TD([[makeQuery(id+"F0.imprint","IMPRINT",EDGE,{"disambiguationData":[TD([[subQ1,1.0]])],"derivedFrom":subQ0}),1.0]])]});}
            var Q66;
            {var subQ0=sQuery(id+"F0.wireOp",EDGE,"E3.1");var subQ1=sQuery(id+"F0.wireOp",EDGE,"E2.1");var subQ2=makeQuery(id+"F0.imprint","INTERSECT",VERTEX,{"derivedFrom":[subQ1,subQ0]});Q66=makeQuery(id+"F0.imprint","IMPRINT",FACE,{"disambiguationData":[TD([[makeQuery(id+"F0.imprint","IMPRINT",EDGE,{"disambiguationData":[TD([[subQ2,-1.0]])],"derivedFrom":subQ1}),-1.0]])]});}
            var Q67;
            {var subQ0=sQuery(id+"F0.wireOp",EDGE,"E4.1");var subQ1=sQuery(id+"F0.wireOp",EDGE,"E2.0");var subQ2=makeQuery(id+"F0.imprint","INTERSECT",VERTEX,{"derivedFrom":[subQ1,subQ0]});Q67=makeQuery(id+"F0.imprint","IMPRINT",FACE,{"disambiguationData":[TD([[makeQuery(id+"F0.imprint","IMPRINT",EDGE,{"disambiguationData":[TD([[subQ2,-1.0]])],"derivedFrom":subQ1}),1.0]])]});}
            var Q68;
            {var subQ0=sQuery(id+"F0.wireOp",EDGE,"E4.2");var subQ1=sQuery(id+"F0.wireOp",EDGE,"E3.1");var subQ2=makeQuery(id+"F0.imprint","INTERSECT",VERTEX,{"derivedFrom":[subQ1,subQ0]});Q68=makeQuery(id+"F0.imprint","IMPRINT",FACE,{"disambiguationData":[TD([[makeQuery(id+"F0.imprint","IMPRINT",EDGE,{"disambiguationData":[TD([[subQ2,-1.0]])],"derivedFrom":subQ1}),-1.0]])]});}
            var Q69;
            {var subQ0=sQuery(id+"F0.wireOp",EDGE,"E5.1");var subQ1=sQuery(id+"F0.wireOp",EDGE,"E2.0");var subQ2=makeQuery(id+"F0.imprint","INTERSECT",VERTEX,{"derivedFrom":[subQ1,subQ0]});Q69=makeQuery(id+"F0.imprint","IMPRINT",FACE,{"disambiguationData":[TD([[makeQuery(id+"F0.imprint","IMPRINT",EDGE,{"disambiguationData":[TD([[subQ2,-1.0]])],"derivedFrom":subQ1}),1.0]])]});}
            var Q70;
            {var subQ0=sQuery(id+"F0.wireOp",EDGE,"E4.2");var subQ1=sQuery(id+"F0.wireOp",EDGE,"E3.0");var subQ2=makeQuery(id+"F0.imprint","INTERSECT",VERTEX,{"derivedFrom":[subQ1,subQ0]});Q70=makeQuery(id+"F0.imprint","IMPRINT",FACE,{"disambiguationData":[TD([[makeQuery(id+"F0.imprint","IMPRINT",EDGE,{"disambiguationData":[TD([[subQ2,-1.0]])],"derivedFrom":subQ1}),1.0]])]});}
            var Q71;
            {var subQ0=sQuery(id+"F0.wireOp",EDGE,"E4.0");var subQ1=sQuery(id+"F0.wireOp",EDGE,"E3.2");var subQ2=makeQuery(id+"F0.imprint","INTERSECT",VERTEX,{"derivedFrom":[subQ1,subQ0]});Q71=makeQuery(id+"F0.imprint","IMPRINT",FACE,{"disambiguationData":[TD([[makeQuery(id+"F0.imprint","IMPRINT",EDGE,{"disambiguationData":[TD([[subQ2,-1.0]])],"derivedFrom":subQ1}),-1.0]])]});}
            var Q72;
            {var subQ0=sQuery(id+"F0.wireOp",EDGE,"E5.2");var subQ1=sQuery(id+"F0.wireOp",EDGE,"E2.0");var subQ2=makeQuery(id+"F0.imprint","INTERSECT",VERTEX,{"derivedFrom":[subQ1,subQ0]});Q72=makeQuery(id+"F0.imprint","IMPRINT",FACE,{"disambiguationData":[TD([[makeQuery(id+"F0.imprint","IMPRINT",EDGE,{"disambiguationData":[TD([[subQ2,-1.0]])],"derivedFrom":subQ1}),-1.0]])]});}
            var Q73;
            {var subQ0=sQuery(id+"F0.wireOp",EDGE,"E3.0");var subQ1=sQuery(id+"F0.wireOp",EDGE,"E2.0");var subQ2=makeQuery(id+"F0.imprint","INTERSECT",VERTEX,{"derivedFrom":[subQ1,subQ0]});Q73=makeQuery(id+"F0.imprint","IMPRINT",FACE,{"disambiguationData":[TD([[makeQuery(id+"F0.imprint","IMPRINT",EDGE,{"disambiguationData":[TD([[subQ2,-1.0]])],"derivedFrom":subQ1}),1.0]])]});}
            var Q74;
            {var subQ0=sQuery(id+"F0.wireOp",EDGE,"E5.0");var subQ1=sQuery(id+"F0.wireOp",EDGE,"E3.1");var subQ2=makeQuery(id+"F0.imprint","INTERSECT",VERTEX,{"derivedFrom":[subQ1,subQ0]});Q74=makeQuery(id+"F0.imprint","IMPRINT",FACE,{"disambiguationData":[TD([[makeQuery(id+"F0.imprint","IMPRINT",EDGE,{"disambiguationData":[TD([[subQ2,-1.0]])],"derivedFrom":subQ1}),1.0]])]});}
            var Q75;
            {var subQ0=sQuery(id+"F0.wireOp",EDGE,"E4.0");var subQ1=sQuery(id+"F0.wireOp",EDGE,"E2.2");var subQ2=makeQuery(id+"F0.imprint","INTERSECT",VERTEX,{"derivedFrom":[subQ1,subQ0]});Q75=makeQuery(id+"F0.imprint","IMPRINT",FACE,{"disambiguationData":[TD([[makeQuery(id+"F0.imprint","IMPRINT",EDGE,{"disambiguationData":[TD([[subQ2,-1.0]])],"derivedFrom":subQ1}),-1.0]])]});}
            var Q76;
            {var subQ0=sQuery(id+"F0.wireOp",EDGE,"E3.0");var subQ1=sQuery(id+"F0.wireOp",EDGE,"E2.1");var subQ2=makeQuery(id+"F0.imprint","INTERSECT",VERTEX,{"derivedFrom":[subQ1,subQ0]});Q76=makeQuery(id+"F0.imprint","IMPRINT",FACE,{"disambiguationData":[TD([[makeQuery(id+"F0.imprint","IMPRINT",EDGE,{"disambiguationData":[TD([[subQ2,-1.0]])],"derivedFrom":subQ1}),-1.0]])]});}
            var Q77;
            {var subQ0=sQuery(id+"F0.wireOp",EDGE,"E5.2");var subQ1=sQuery(id+"F0.wireOp",EDGE,"E2.1");var subQ2=makeQuery(id+"F0.imprint","INTERSECT",VERTEX,{"derivedFrom":[subQ1,subQ0]});Q77=makeQuery(id+"F0.imprint","IMPRINT",FACE,{"disambiguationData":[TD([[makeQuery(id+"F0.imprint","IMPRINT",EDGE,{"disambiguationData":[TD([[subQ2,-1.0]])],"derivedFrom":subQ1}),-1.0]])]});}
            var Q78;
            {var subQ0=sQuery(id+"F0.wireOp",EDGE,"E5.0");var subQ1=sQuery(id+"F0.wireOp",EDGE,"E2.2");var subQ2=makeQuery(id+"F0.imprint","INTERSECT",VERTEX,{"derivedFrom":[subQ1,subQ0]});Q78=makeQuery(id+"F0.imprint","IMPRINT",FACE,{"disambiguationData":[TD([[makeQuery(id+"F0.imprint","IMPRINT",EDGE,{"disambiguationData":[TD([[subQ2,-1.0]])],"derivedFrom":subQ1}),1.0]])]});}
            var Q79;
            {var subQ0=sQuery(id+"F0.wireOp",EDGE,"E4.0");var subQ1=sQuery(id+"F0.wireOp",EDGE,"E3.1");var subQ2=makeQuery(id+"F0.imprint","INTERSECT",VERTEX,{"derivedFrom":[subQ1,subQ0]});Q79=makeQuery(id+"F0.imprint","IMPRINT",FACE,{"disambiguationData":[TD([[makeQuery(id+"F0.imprint","IMPRINT",EDGE,{"disambiguationData":[TD([[subQ2,-1.0]])],"derivedFrom":subQ1}),1.0]])]});}
            var Q80;
            {var subQ0=sQuery(id+"F0.wireOp",EDGE,"E4.2");var subQ1=makeQuery(id+"F0.imprint","INTERSECT",VERTEX,{"derivedFrom":[sQuery(id+"F0.wireOp",EDGE,"E1"),subQ0]});Q80=makeQuery(id+"F0.imprint","IMPRINT",FACE,{"disambiguationData":[TD([[makeQuery(id+"F0.imprint","IMPRINT",EDGE,{"disambiguationData":[TD([[subQ1,1.0]])],"derivedFrom":subQ0}),1.0]])]});}
            var Q81;
            {var subQ0=sQuery(id+"F0.wireOp",EDGE,"E7.1");var subQ1=sQuery(id+"F0.wireOp",EDGE,"E2.2");var subQ2=makeQuery(id+"F0.imprint","INTERSECT",VERTEX,{"derivedFrom":[subQ1,subQ0]});Q81=makeQuery(id+"F0.imprint","IMPRINT",FACE,{"disambiguationData":[TD([[makeQuery(id+"F0.imprint","IMPRINT",EDGE,{"disambiguationData":[TD([[subQ2,-1.0]])],"derivedFrom":subQ1}),-1.0]])]});}
            var Q82;
            {var subQ0=sQuery(id+"F0.wireOp",EDGE,"E4.1");var subQ1=sQuery(id+"F0.wireOp",EDGE,"E3.0");var subQ2=makeQuery(id+"F0.imprint","INTERSECT",VERTEX,{"derivedFrom":[subQ1,subQ0]});Q82=makeQuery(id+"F0.imprint","IMPRINT",FACE,{"disambiguationData":[TD([[makeQuery(id+"F0.imprint","IMPRINT",EDGE,{"disambiguationData":[TD([[subQ2,-1.0]])],"derivedFrom":subQ1}),-1.0]])]});}
            var Q83;
            {var subQ0=sQuery(id+"F0.wireOp",EDGE,"E3.1");var subQ1=sQuery(id+"F0.wireOp",EDGE,"E2.1");var subQ2=makeQuery(id+"F0.imprint","INTERSECT",VERTEX,{"derivedFrom":[subQ1,subQ0]});Q83=makeQuery(id+"F0.imprint","IMPRINT",FACE,{"disambiguationData":[TD([[makeQuery(id+"F0.imprint","IMPRINT",EDGE,{"disambiguationData":[TD([[subQ2,-1.0]])],"derivedFrom":subQ1}),1.0]])]});}
            var Q84;
            {var subQ0=sQuery(id+"F0.wireOp",EDGE,"E3.2");var subQ1=sQuery(id+"F0.wireOp",EDGE,"E2.2");var subQ2=makeQuery(id+"F0.imprint","INTERSECT",VERTEX,{"derivedFrom":[subQ1,subQ0]});Q84=makeQuery(id+"F0.imprint","IMPRINT",FACE,{"disambiguationData":[TD([[makeQuery(id+"F0.imprint","IMPRINT",EDGE,{"disambiguationData":[TD([[subQ2,-1.0]])],"derivedFrom":subQ1}),1.0]])]});}
            var Q85;
            {var subQ0=sQuery(id+"F0.wireOp",EDGE,"E3.1");var subQ1=makeQuery(id+"F0.imprint","INTERSECT",VERTEX,{"derivedFrom":[sQuery(id+"F0.wireOp",EDGE,"E1"),subQ0]});Q85=makeQuery(id+"F0.imprint","IMPRINT",FACE,{"disambiguationData":[TD([[makeQuery(id+"F0.imprint","IMPRINT",EDGE,{"disambiguationData":[TD([[subQ1,1.0]])],"derivedFrom":subQ0}),1.0]])]});}
            var Q86;
            {var subQ0=sQuery(id+"F0.wireOp",EDGE,"E5.0");var subQ1=sQuery(id+"F0.wireOp",EDGE,"E2.1");var subQ2=makeQuery(id+"F0.imprint","INTERSECT",VERTEX,{"derivedFrom":[subQ1,subQ0]});Q86=makeQuery(id+"F0.imprint","IMPRINT",FACE,{"disambiguationData":[TD([[makeQuery(id+"F0.imprint","IMPRINT",EDGE,{"disambiguationData":[TD([[subQ2,-1.0]])],"derivedFrom":subQ1}),-1.0]])]});}
            var Q87;
            {var subQ0=sQuery(id+"F0.wireOp",EDGE,"E5.1");var subQ1=sQuery(id+"F0.wireOp",EDGE,"E2.2");var subQ2=makeQuery(id+"F0.imprint","INTERSECT",VERTEX,{"derivedFrom":[subQ1,subQ0]});Q87=makeQuery(id+"F0.imprint","IMPRINT",FACE,{"disambiguationData":[TD([[makeQuery(id+"F0.imprint","IMPRINT",EDGE,{"disambiguationData":[TD([[subQ2,-1.0]])],"derivedFrom":subQ1}),-1.0]])]});}
            var Q88;
            {var subQ0=sQuery(id+"F0.wireOp",EDGE,"E3.0");var subQ1=sQuery(id+"F0.wireOp",EDGE,"E2.0");var subQ2=makeQuery(id+"F0.imprint","INTERSECT",VERTEX,{"derivedFrom":[subQ1,subQ0]});Q88=makeQuery(id+"F0.imprint","IMPRINT",FACE,{"disambiguationData":[TD([[makeQuery(id+"F0.imprint","IMPRINT",EDGE,{"disambiguationData":[TD([[subQ2,-1.0]])],"derivedFrom":subQ1}),-1.0]])]});}
            var Q89;
            {var subQ0=sQuery(id+"F0.wireOp",EDGE,"E4.2");var subQ1=sQuery(id+"F0.wireOp",EDGE,"E1");var subQ2=makeQuery(id+"F0.imprint","INTERSECT",VERTEX,{"derivedFrom":[subQ1,subQ0]});Q89=makeQuery(id+"F0.imprint","IMPRINT",FACE,{"disambiguationData":[TD([[makeQuery(id+"F0.imprint","IMPRINT",EDGE,{"disambiguationData":[TD([[subQ2,1.0]])],"derivedFrom":subQ1}),-1.0]])]});}
            var Q90;
            {var subQ0=sQuery(id+"F0.wireOp",EDGE,"E2.1");var subQ1=sQuery(id+"F0.wireOp",EDGE,"E1");var subQ2=makeQuery(id+"F0.imprint","INTERSECT",VERTEX,{"derivedFrom":[subQ1,subQ0]});Q90=makeQuery(id+"F0.imprint","IMPRINT",FACE,{"disambiguationData":[TD([[makeQuery(id+"F0.imprint","IMPRINT",EDGE,{"disambiguationData":[TD([[subQ2,-1.0]])],"derivedFrom":subQ1}),-1.0]])]});}
            var Q91;
            {var subQ0=sQuery(id+"F0.wireOp",EDGE,"E2.0");var subQ1=sQuery(id+"F0.wireOp",EDGE,"E1");var subQ2=makeQuery(id+"F0.imprint","INTERSECT",VERTEX,{"derivedFrom":[subQ1,subQ0]});Q91=makeQuery(id+"F0.imprint","IMPRINT",FACE,{"disambiguationData":[TD([[makeQuery(id+"F0.imprint","IMPRINT",EDGE,{"disambiguationData":[TD([[subQ2,-1.0]])],"derivedFrom":subQ1}),-1.0]])]});}
            var Q92;
            {var subQ0=sQuery(id+"F0.wireOp",EDGE,"E5.2");var subQ1=sQuery(id+"F0.wireOp",EDGE,"E1");var subQ2=makeQuery(id+"F0.imprint","INTERSECT",VERTEX,{"derivedFrom":[subQ1,subQ0]});Q92=makeQuery(id+"F0.imprint","IMPRINT",FACE,{"disambiguationData":[TD([[makeQuery(id+"F0.imprint","IMPRINT",EDGE,{"disambiguationData":[TD([[subQ2,-1.0]])],"derivedFrom":subQ1}),-1.0]])]});}
            var Q93;
            {var subQ0=sQuery(id+"F0.wireOp",EDGE,"E3.2");var subQ1=sQuery(id+"F0.wireOp",EDGE,"E1");var subQ2=makeQuery(id+"F0.imprint","INTERSECT",VERTEX,{"derivedFrom":[subQ1,subQ0]});Q93=makeQuery(id+"F0.imprint","IMPRINT",FACE,{"disambiguationData":[TD([[makeQuery(id+"F0.imprint","IMPRINT",EDGE,{"disambiguationData":[TD([[subQ2,-1.0]])],"derivedFrom":subQ1}),-1.0]])]});}
            var Q94;
            {var subQ0=sQuery(id+"F0.wireOp",EDGE,"E6.0");var subQ1=sQuery(id+"F0.wireOp",EDGE,"E1");var subQ2=makeQuery(id+"F0.imprint","INTERSECT",VERTEX,{"derivedFrom":[subQ1,subQ0]});Q94=makeQuery(id+"F0.imprint","IMPRINT",FACE,{"disambiguationData":[TD([[makeQuery(id+"F0.imprint","IMPRINT",EDGE,{"disambiguationData":[TD([[subQ2,-1.0]])],"derivedFrom":subQ1}),-1.0]])]});}
            var Q95;
            {var subQ0=sQuery(id+"F0.wireOp",EDGE,"E5.1");var subQ1=sQuery(id+"F0.wireOp",EDGE,"E1");var subQ2=makeQuery(id+"F0.imprint","INTERSECT",VERTEX,{"derivedFrom":[subQ1,subQ0]});Q95=makeQuery(id+"F0.imprint","IMPRINT",FACE,{"disambiguationData":[TD([[makeQuery(id+"F0.imprint","IMPRINT",EDGE,{"disambiguationData":[TD([[subQ2,-1.0]])],"derivedFrom":subQ1}),-1.0]])]});}
            var Q96;
            {var subQ0=sQuery(id+"F0.wireOp",EDGE,"E7.2");var subQ1=sQuery(id+"F0.wireOp",EDGE,"E1");var subQ2=makeQuery(id+"F0.imprint","INTERSECT",VERTEX,{"derivedFrom":[subQ1,subQ0]});Q96=makeQuery(id+"F0.imprint","IMPRINT",FACE,{"disambiguationData":[TD([[makeQuery(id+"F0.imprint","IMPRINT",EDGE,{"disambiguationData":[TD([[subQ2,-1.0]])],"derivedFrom":subQ1}),-1.0]])]});}
            var Q97;
            {var subQ0=sQuery(id+"F0.wireOp",EDGE,"E4.0");var subQ1=sQuery(id+"F0.wireOp",EDGE,"E1");var subQ2=makeQuery(id+"F0.imprint","INTERSECT",VERTEX,{"derivedFrom":[subQ1,subQ0]});Q97=makeQuery(id+"F0.imprint","IMPRINT",FACE,{"disambiguationData":[TD([[makeQuery(id+"F0.imprint","IMPRINT",EDGE,{"disambiguationData":[TD([[subQ2,-1.0]])],"derivedFrom":subQ1}),-1.0]])]});}
            var Q98;
            {var subQ0=sQuery(id+"F0.wireOp",EDGE,"E3.0");var subQ1=makeQuery(id+"F0.imprint","INTERSECT",VERTEX,{"derivedFrom":[sQuery(id+"F0.wireOp",EDGE,"E1"),subQ0]});Q98=makeQuery(id+"F0.imprint","IMPRINT",FACE,{"disambiguationData":[TD([[makeQuery(id+"F0.imprint","IMPRINT",EDGE,{"disambiguationData":[TD([[subQ1,1.0]])],"derivedFrom":subQ0}),1.0]])]});}
            var Q99;
            {var subQ0=sQuery(id+"F0.wireOp",EDGE,"E2.0");var subQ1=makeQuery(id+"F0.imprint","INTERSECT",VERTEX,{"derivedFrom":[sQuery(id+"F0.wireOp",EDGE,"E1"),subQ0]});Q99=makeQuery(id+"F0.imprint","IMPRINT",FACE,{"disambiguationData":[TD([[makeQuery(id+"F0.imprint","IMPRINT",EDGE,{"disambiguationData":[TD([[subQ1,1.0]])],"derivedFrom":subQ0}),1.0]])]});}
            var Q100;
            {var subQ0=sQuery(id+"F0.wireOp",EDGE,"E3.1");var subQ1=sQuery(id+"F0.wireOp",EDGE,"E1");var subQ2=makeQuery(id+"F0.imprint","INTERSECT",VERTEX,{"derivedFrom":[subQ1,subQ0]});Q100=makeQuery(id+"F0.imprint","IMPRINT",FACE,{"disambiguationData":[TD([[makeQuery(id+"F0.imprint","IMPRINT",EDGE,{"disambiguationData":[TD([[subQ2,-1.0]])],"derivedFrom":subQ1}),-1.0]])]});}
            var Q101;
            {var subQ0=sQuery(id+"F0.wireOp",EDGE,"E5.0");var subQ1=sQuery(id+"F0.wireOp",EDGE,"E3.1");var subQ2=makeQuery(id+"F0.imprint","INTERSECT",VERTEX,{"derivedFrom":[subQ1,subQ0]});Q101=makeQuery(id+"F0.imprint","IMPRINT",FACE,{"disambiguationData":[TD([[makeQuery(id+"F0.imprint","IMPRINT",EDGE,{"disambiguationData":[TD([[subQ2,-1.0]])],"derivedFrom":subQ1}),-1.0]])]});}
            var Q102;
            {var subQ0=sQuery(id+"F0.wireOp",EDGE,"E4.1");var subQ1=sQuery(id+"F0.wireOp",EDGE,"E1");var subQ2=makeQuery(id+"F0.imprint","INTERSECT",VERTEX,{"derivedFrom":[subQ1,subQ0]});Q102=makeQuery(id+"F0.imprint","IMPRINT",FACE,{"disambiguationData":[TD([[makeQuery(id+"F0.imprint","IMPRINT",EDGE,{"disambiguationData":[TD([[subQ2,-1.0]])],"derivedFrom":subQ1}),-1.0]])]});}
            var Q103;
            {var subQ0=sQuery(id+"F0.wireOp",EDGE,"E2.2");var subQ1=sQuery(id+"F0.wireOp",EDGE,"E1");var subQ2=makeQuery(id+"F0.imprint","INTERSECT",VERTEX,{"derivedFrom":[subQ1,subQ0]});Q103=makeQuery(id+"F0.imprint","IMPRINT",FACE,{"disambiguationData":[TD([[makeQuery(id+"F0.imprint","IMPRINT",EDGE,{"disambiguationData":[TD([[subQ2,-1.0]])],"derivedFrom":subQ1}),-1.0]])]});}
            var Q104;
            {var subQ0=sQuery(id+"F0.wireOp",EDGE,"E5.2");var subQ1=sQuery(id+"F0.wireOp",EDGE,"E1");var subQ2=makeQuery(id+"F0.imprint","INTERSECT",VERTEX,{"derivedFrom":[subQ1,subQ0]});Q104=makeQuery(id+"F0.imprint","IMPRINT",FACE,{"disambiguationData":[TD([[makeQuery(id+"F0.imprint","IMPRINT",EDGE,{"disambiguationData":[TD([[subQ2,1.0]])],"derivedFrom":subQ1}),-1.0]])]});}
            var Q105;
            {var subQ0=sQuery(id+"F0.wireOp",EDGE,"E7.1");var subQ1=sQuery(id+"F0.wireOp",EDGE,"E1");var subQ2=makeQuery(id+"F0.imprint","INTERSECT",VERTEX,{"derivedFrom":[subQ1,subQ0]});Q105=makeQuery(id+"F0.imprint","IMPRINT",FACE,{"disambiguationData":[TD([[makeQuery(id+"F0.imprint","IMPRINT",EDGE,{"disambiguationData":[TD([[subQ2,-1.0]])],"derivedFrom":subQ1}),-1.0]])]});}
            var Q106;
            {var subQ0=sQuery(id+"F0.wireOp",EDGE,"E7.0");var subQ1=sQuery(id+"F0.wireOp",EDGE,"E1");var subQ2=makeQuery(id+"F0.imprint","INTERSECT",VERTEX,{"derivedFrom":[subQ1,subQ0]});Q106=makeQuery(id+"F0.imprint","IMPRINT",FACE,{"disambiguationData":[TD([[makeQuery(id+"F0.imprint","IMPRINT",EDGE,{"disambiguationData":[TD([[subQ2,-1.0]])],"derivedFrom":subQ1}),-1.0]])]});}
            var Q107;
            {var subQ0=sQuery(id+"F0.wireOp",EDGE,"E5.0");var subQ1=sQuery(id+"F0.wireOp",EDGE,"E1");var subQ2=makeQuery(id+"F0.imprint","INTERSECT",VERTEX,{"derivedFrom":[subQ1,subQ0]});Q107=makeQuery(id+"F0.imprint","IMPRINT",FACE,{"disambiguationData":[TD([[makeQuery(id+"F0.imprint","IMPRINT",EDGE,{"disambiguationData":[TD([[subQ2,-1.0]])],"derivedFrom":subQ1}),-1.0]])]});}
            var Q108;
            {var subQ0=sQuery(id+"F0.wireOp",EDGE,"E3.0");var subQ1=sQuery(id+"F0.wireOp",EDGE,"E1");var subQ2=makeQuery(id+"F0.imprint","INTERSECT",VERTEX,{"derivedFrom":[subQ1,subQ0]});Q108=makeQuery(id+"F0.imprint","IMPRINT",FACE,{"disambiguationData":[TD([[makeQuery(id+"F0.imprint","IMPRINT",EDGE,{"disambiguationData":[TD([[subQ2,-1.0]])],"derivedFrom":subQ1}),-1.0]])]});}
            var Q109;
            {var subQ0=sQuery(id+"F0.wireOp",EDGE,"E6.1");var subQ1=sQuery(id+"F0.wireOp",EDGE,"E1");var subQ2=makeQuery(id+"F0.imprint","INTERSECT",VERTEX,{"derivedFrom":[subQ1,subQ0]});Q109=makeQuery(id+"F0.imprint","IMPRINT",FACE,{"disambiguationData":[TD([[makeQuery(id+"F0.imprint","IMPRINT",EDGE,{"disambiguationData":[TD([[subQ2,-1.0]])],"derivedFrom":subQ1}),-1.0]])]});}
            extrude(context, id + "F1", {"entities" : qUnion([Q0, Q1, Q2, Q3, Q4, Q5, Q6, Q7, Q8, Q9, Q10, Q11, Q12, Q13, Q14, Q15, Q16, Q17, Q18, Q19, Q20, Q21, Q22, Q23, Q24, Q25, Q26, Q27, Q28, Q29, Q30, Q31, Q32, Q33, Q34, Q35, Q36, Q37, Q38, Q39, Q40, Q41, Q42, Q43, Q44, Q45, Q46, Q47, Q48, Q49, Q50, Q51, Q52, Q53, Q54, Q55, Q56, Q57, Q58, Q59, Q60, Q61, Q62, Q63, Q64, Q65, Q66, Q67, Q68, Q69, Q70, Q71, Q72, Q73, Q74, Q75, Q76, Q77, Q78, Q79, Q80, Q81, Q82, Q83, Q84, Q85, Q86, Q87, Q88, Q89, Q90, Q91, Q92, Q93, Q94, Q95, Q96, Q97, Q98, Q99, Q100, Q101, Q102, Q103, Q104, Q105, Q106, Q107, Q108, Q109]), "depth" : 40 * mm, "offsetDistance" : 25 * mm});
        }
        {
            var Q0;
            Q0=makeQuery(id+"F1.opExtrude","CAP_FACE",FACE,{"disambiguationData":[OSD([sQuery(id+"F0.wireOp",EDGE,"E2.0"),sQuery(id+"F0.wireOp",EDGE,"E2.1"),sQuery(id+"F0.wireOp",EDGE,"E2.2"),sQuery(id+"F0.wireOp",EDGE,"E3.0"),sQuery(id+"F0.wireOp",EDGE,"E3.1"),sQuery(id+"F0.wireOp",EDGE,"E3.2"),sQuery(id+"F0.wireOp",EDGE,"E4.0"),sQuery(id+"F0.wireOp",EDGE,"E4.1"),sQuery(id+"F0.wireOp",EDGE,"E4.2"),sQuery(id+"F0.wireOp",EDGE,"E5.0"),sQuery(id+"F0.wireOp",EDGE,"E5.1"),sQuery(id+"F0.wireOp",EDGE,"E5.2"),sQuery(id+"F0.wireOp",EDGE,"E6.0"),sQuery(id+"F0.wireOp",EDGE,"E6.1"),sQuery(id+"F0.wireOp",EDGE,"E6.2"),sQuery(id+"F0.wireOp",EDGE,"E7.0"),sQuery(id+"F0.wireOp",EDGE,"E7.1"),sQuery(id+"F0.wireOp",EDGE,"E7.2")])],"isStart":false});
            var sketch = newSketch(context, id + "F2", { "sketchPlane" : qUnion([Q0])});
            skCircle(sketch, "E8", {"center": v(0, 0) * mm, "radius": 15 * mm});
            skSolve(sketch);
        }
        {
            var Q0;
            Q0 = qSketchRegion(id + "F2", true);
            extrude(context, id + "F3", {"entities" : qUnion([Q0]), "operationType" : NewBodyOperationType.REMOVE, "oppositeDirection" : true, "depth" : 40 * mm, "offsetDistance" : 25 * mm});
        }
        {
            var Q0;
            Q0=makeQuery(id+"F1.opExtrude","CAP_FACE",FACE,{"disambiguationData":[OSD([sQuery(id+"F0.wireOp",EDGE,"E2.0"),sQuery(id+"F0.wireOp",EDGE,"E2.1"),sQuery(id+"F0.wireOp",EDGE,"E2.2"),sQuery(id+"F0.wireOp",EDGE,"E3.0"),sQuery(id+"F0.wireOp",EDGE,"E3.1"),sQuery(id+"F0.wireOp",EDGE,"E3.2"),sQuery(id+"F0.wireOp",EDGE,"E4.0"),sQuery(id+"F0.wireOp",EDGE,"E4.1"),sQuery(id+"F0.wireOp",EDGE,"E4.2"),sQuery(id+"F0.wireOp",EDGE,"E5.0"),sQuery(id+"F0.wireOp",EDGE,"E5.1"),sQuery(id+"F0.wireOp",EDGE,"E5.2"),sQuery(id+"F0.wireOp",EDGE,"E6.0"),sQuery(id+"F0.wireOp",EDGE,"E6.1"),sQuery(id+"F0.wireOp",EDGE,"E6.2"),sQuery(id+"F0.wireOp",EDGE,"E7.0"),sQuery(id+"F0.wireOp",EDGE,"E7.1"),sQuery(id+"F0.wireOp",EDGE,"E7.2")])],"isStart":true});
            var sketch = newSketch(context, id + "F4", { "sketchPlane" : qUnion([Q0])});
            skLineSegment(sketch, "E9", {"start": v(-54.82, 19.95) * mm, "end": v(-89.15, 42.29) * mm});
            skLineSegment(sketch, "E10", {"start": v(-89.15, 42.29) * mm, "end": v(-77.95, 59.5) * mm});
            skLineSegment(sketch, "E11", {"start": v(-77.95, 59.5) * mm, "end": v(-44.7, 37.5) * mm});
            skSolve(sketch);
        }
        {
            var Q0;
            Q0=makeQuery(id+"F4.imprint","IMPRINT",FACE,{"disambiguationData":[TD([[makeQuery(id+"F4.imprint","IMPRINT",EDGE,{"derivedFrom":sQuery(id+"F4.wireOp",EDGE,"E9")}),-1.0]])]});
            extrude(context, id + "F5", {"entities" : qUnion([Q0]), "oppositeDirection" : true, "depth" : 40 * mm, "offsetDistance" : 25 * mm});
        }
        {
            var Q0;
            Q0=makeQuery(id+"F5.opExtrude","SWEPT_BODY",BODY,{"disambiguationData":[OSD([sQuery(id+"F0.wireOp",EDGE,"E2.0"),sQuery(id+"F0.wireOp",EDGE,"E2.1"),sQuery(id+"F4.wireOp",EDGE,"E9"),sQuery(id+"F4.wireOp",EDGE,"E10"),sQuery(id+"F4.wireOp",EDGE,"E11")])]});
            deleteBodies(context, id + "F6", {"entities" : qUnion([Q0])});
        }
        {
            var Q0;
            Q0=makeQuery(id+"F1.opExtrude","CAP_FACE",FACE,{"disambiguationData":[OSD([sQuery(id+"F0.wireOp",EDGE,"E2.0"),sQuery(id+"F0.wireOp",EDGE,"E2.1"),sQuery(id+"F0.wireOp",EDGE,"E2.2"),sQuery(id+"F0.wireOp",EDGE,"E3.0"),sQuery(id+"F0.wireOp",EDGE,"E3.1"),sQuery(id+"F0.wireOp",EDGE,"E3.2"),sQuery(id+"F0.wireOp",EDGE,"E4.0"),sQuery(id+"F0.wireOp",EDGE,"E4.1"),sQuery(id+"F0.wireOp",EDGE,"E4.2"),sQuery(id+"F0.wireOp",EDGE,"E5.0"),sQuery(id+"F0.wireOp",EDGE,"E5.1"),sQuery(id+"F0.wireOp",EDGE,"E5.2"),sQuery(id+"F0.wireOp",EDGE,"E6.0"),sQuery(id+"F0.wireOp",EDGE,"E6.1"),sQuery(id+"F0.wireOp",EDGE,"E6.2"),sQuery(id+"F0.wireOp",EDGE,"E7.0"),sQuery(id+"F0.wireOp",EDGE,"E7.1"),sQuery(id+"F0.wireOp",EDGE,"E7.2")])],"isStart":true});
            var sketch = newSketch(context, id + "F7", { "sketchPlane" : qUnion([Q0])});
            skLineSegment(sketch, "E12", {"start": v(-73.86, 13.02) * mm, "end": v(-5.5, -13.95) * mm});
            skLineSegment(sketch, "E13", {"start": v(-5.5, -13.95) * mm, "end": v(5.14, 13.02) * mm});
            skLineSegment(sketch, "E14", {"start": v(5.14, 13.02) * mm, "end": v(-64.95, 37.5) * mm});
            skLineSegment(sketch, "E15", {"start": v(-73.86, 13.02) * mm, "end": v(-401.62, 135.8) * mm});
            skLineSegment(sketch, "E16", {"start": v(-64.95, 37.5) * mm, "end": v(-392.7, 160.28) * mm});
            skLineSegment(sketch, "E17", {"start": v(-401.62, 135.8) * mm, "end": v(-392.7, 160.28) * mm});
            skSolve(sketch);
        }
        {
            var Q0;
            Q0=makeQuery(id+"F7.imprint","IMPRINT",FACE,{"disambiguationData":[TD([[makeQuery(id+"F7.imprint","IMPRINT",EDGE,{"derivedFrom":sQuery(id+"F7.wireOp",EDGE,"E15")}),-1.0]])]});
            extrude(context, id + "F8", {"entities" : qUnion([Q0]), "operationType" : NewBodyOperationType.ADD, "oppositeDirection" : true, "depth" : 40 * mm, "offsetDistance" : 25 * mm});
        }
        {
            var Q0;
            {var subQ0=sQuery(id+"F0.wireOp",EDGE,"E2.1");var subQ1=sQuery(id+"F0.wireOp",EDGE,"E2.0");Q0=makeQuery(id+"F8.boolean.opBoolean","MERGE",EDGE,{"derivedFrom":[makeQuery(id+"F1.opExtrude","SWEPT_EDGE",EDGE,{"disambiguationData":[OSD([subQ1,subQ0])]}),makeQuery(id+"F8.opExtrude","SWEPT_EDGE",EDGE,{"disambiguationData":[OSD([subQ1,subQ0,sQuery(id+"F7.wireOp",EDGE,"E14"),sQuery(id+"F7.wireOp",EDGE,"E16")])]})]});}
            var Q1;
            {var subQ0=sQuery(id+"F0.wireOp",EDGE,"E7.2");var subQ1=sQuery(id+"F0.wireOp",EDGE,"E7.0");Q1=makeQuery(id+"F8.boolean.opBoolean","MERGE",EDGE,{"derivedFrom":[makeQuery(id+"F1.opExtrude","SWEPT_EDGE",EDGE,{"disambiguationData":[OSD([subQ1,subQ0])]}),makeQuery(id+"F8.opExtrude","SWEPT_EDGE",EDGE,{"disambiguationData":[OSD([subQ1,subQ0,sQuery(id+"F7.wireOp",EDGE,"E12"),sQuery(id+"F7.wireOp",EDGE,"E15")])]})]});}
            fillet(context, id + "F9", {"entities" : qUnion([Q0, Q1]), "radius" : 100 * mm, "tangentPropagation" : true, "allowEdgeOverflow" : false});
        }
        {
            var Q0;
            Q0=makeQuery(id+"F8.opExtrude","SWEPT_FACE",FACE,{"disambiguationData":[OSD([sQuery(id+"F7.wireOp",EDGE,"E17")])]});
            var sketch = newSketch(context, id + "F10", { "sketchPlane" : qUnion([Q0])});
            skLineSegment(sketch, "E18.bottom", {"start": v(-30, 25.55) * mm, "end": v(-10, 25.55) * mm});
            skLineSegment(sketch, "E18.top", {"start": v(-30, -20.83) * mm, "end": v(-10, -20.83) * mm});
            skLineSegment(sketch, "E18.left", {"start": v(-30, 25.55) * mm, "end": v(-30, -20.83) * mm});
            skLineSegment(sketch, "E18.right", {"start": v(-10, 25.55) * mm, "end": v(-10, -20.83) * mm});
            skSolve(sketch);
        }
        {
            var Q0;
            Q0 = qSketchRegion(id + "F10", true);
            extrude(context, id + "F11", {"entities" : qUnion([Q0]), "operationType" : NewBodyOperationType.REMOVE, "oppositeDirection" : true, "depth" : 100 * mm, "offsetDistance" : 25 * mm});
        }
        {
            var Q0;
            {var subQ0=sQuery(id+"F7.wireOp",EDGE,"E17");var subQ1=sQuery(id+"F7.wireOp",EDGE,"E15");Q0=makeQuery(id+"F11.boolean.opBoolean","SPLIT",EDGE,{"disambiguationData":[TD([makeQuery(id+"F11.opExtrude","SWEPT_FACE",FACE,{"disambiguationData":[OSD([sQuery(id+"F10.wireOp",EDGE,"E18.right")])]})])],"derivedFrom":makeQuery(id+"F8.opExtrude","SWEPT_EDGE",EDGE,{"disambiguationData":[OSD([subQ1,subQ0])]})});}
            var Q1;
            {var subQ0=sQuery(id+"F7.wireOp",EDGE,"E17");var subQ1=sQuery(id+"F7.wireOp",EDGE,"E15");Q1=makeQuery(id+"F11.boolean.opBoolean","SPLIT",EDGE,{"disambiguationData":[TD([makeQuery(id+"F11.opExtrude","SWEPT_FACE",FACE,{"disambiguationData":[OSD([sQuery(id+"F10.wireOp",EDGE,"E18.left")])]})])],"derivedFrom":makeQuery(id+"F8.opExtrude","SWEPT_EDGE",EDGE,{"disambiguationData":[OSD([subQ1,subQ0])]})});}
            var Q2;
            {var subQ0=sQuery(id+"F7.wireOp",EDGE,"E17");var subQ1=sQuery(id+"F7.wireOp",EDGE,"E16");Q2=makeQuery(id+"F11.boolean.opBoolean","SPLIT",EDGE,{"disambiguationData":[TD([makeQuery(id+"F11.opExtrude","SWEPT_FACE",FACE,{"disambiguationData":[OSD([sQuery(id+"F10.wireOp",EDGE,"E18.left")])]})])],"derivedFrom":makeQuery(id+"F8.opExtrude","SWEPT_EDGE",EDGE,{"disambiguationData":[OSD([subQ1,subQ0])]})});}
            var Q3;
            {var subQ0=sQuery(id+"F7.wireOp",EDGE,"E17");var subQ1=sQuery(id+"F7.wireOp",EDGE,"E16");Q3=makeQuery(id+"F11.boolean.opBoolean","SPLIT",EDGE,{"disambiguationData":[TD([makeQuery(id+"F11.opExtrude","SWEPT_FACE",FACE,{"disambiguationData":[OSD([sQuery(id+"F10.wireOp",EDGE,"E18.right")])]})])],"derivedFrom":makeQuery(id+"F8.opExtrude","SWEPT_EDGE",EDGE,{"disambiguationData":[OSD([subQ1,subQ0])]})});}
            fillet(context, id + "F12", {"entities" : qUnion([Q0, Q1, Q2, Q3]), "radius" : 10 * mm, "tangentPropagation" : true, "allowEdgeOverflow" : false});
        }
        {
            var Q0;
            {var subQ0=sQuery(id+"F0.wireOp",EDGE,"E7.2");var subQ1=sQuery(id+"F0.wireOp",EDGE,"E2.1");Q0=makeQuery(id+"F8.boolean.opBoolean","MERGE",FACE,{"derivedFrom":[makeQuery(id+"F1.opExtrude","CAP_FACE",FACE,{"disambiguationData":[OSD([sQuery(id+"F0.wireOp",EDGE,"E2.0"),subQ1,sQuery(id+"F0.wireOp",EDGE,"E2.2"),sQuery(id+"F0.wireOp",EDGE,"E3.0"),sQuery(id+"F0.wireOp",EDGE,"E3.1"),sQuery(id+"F0.wireOp",EDGE,"E3.2"),sQuery(id+"F0.wireOp",EDGE,"E4.0"),sQuery(id+"F0.wireOp",EDGE,"E4.1"),sQuery(id+"F0.wireOp",EDGE,"E4.2"),sQuery(id+"F0.wireOp",EDGE,"E5.0"),sQuery(id+"F0.wireOp",EDGE,"E5.1"),sQuery(id+"F0.wireOp",EDGE,"E5.2"),sQuery(id+"F0.wireOp",EDGE,"E6.0"),sQuery(id+"F0.wireOp",EDGE,"E6.1"),sQuery(id+"F0.wireOp",EDGE,"E6.2"),sQuery(id+"F0.wireOp",EDGE,"E7.0"),sQuery(id+"F0.wireOp",EDGE,"E7.1"),subQ0])],"isStart":true}),makeQuery(id+"F8.opExtrude","CAP_FACE",FACE,{"disambiguationData":[OSD([subQ1,subQ0,sQuery(id+"F7.wireOp",EDGE,"E15"),sQuery(id+"F7.wireOp",EDGE,"E16"),sQuery(id+"F7.wireOp",EDGE,"E17")])],"isStart":true})]});}
            var sketch = newSketch(context, id + "F13", { "sketchPlane" : qUnion([Q0])});
            skPoint(sketch, "E19", {"position": v(-369.06, 137.54) * mm});
            skPoint(sketch, "E20", {"position": v(-340.97, 127.02) * mm});
            skSolve(sketch);
        }
        {
            var Q0;
            Q0=sQuery(id+"F13.wireOp",VERTEX,"E19");
            var Q1;
            Q1=sQuery(id+"F13.wireOp",VERTEX,"E20");
            var Q2;
            Q2=makeQuery(id+"F1.opExtrude","SWEPT_BODY",BODY,{"disambiguationData":[OSD([sQuery(id+"F0.wireOp",EDGE,"E2.0"),sQuery(id+"F0.wireOp",EDGE,"E2.1"),sQuery(id+"F0.wireOp",EDGE,"E2.2"),sQuery(id+"F0.wireOp",EDGE,"E3.0"),sQuery(id+"F0.wireOp",EDGE,"E3.1"),sQuery(id+"F0.wireOp",EDGE,"E3.2"),sQuery(id+"F0.wireOp",EDGE,"E4.0"),sQuery(id+"F0.wireOp",EDGE,"E4.1"),sQuery(id+"F0.wireOp",EDGE,"E4.2"),sQuery(id+"F0.wireOp",EDGE,"E5.0"),sQuery(id+"F0.wireOp",EDGE,"E5.1"),sQuery(id+"F0.wireOp",EDGE,"E5.2"),sQuery(id+"F0.wireOp",EDGE,"E6.0"),sQuery(id+"F0.wireOp",EDGE,"E6.1"),sQuery(id+"F0.wireOp",EDGE,"E6.2"),sQuery(id+"F0.wireOp",EDGE,"E7.0"),sQuery(id+"F0.wireOp",EDGE,"E7.1"),sQuery(id+"F0.wireOp",EDGE,"E7.2")])]});
            hole(context, id + "F14", {"style" : HoleStyle.SIMPLE, "endStyle" : HoleEndStyle.BLIND, "holeDiameter" : 10 * mm, "majorDiameter" : 5 * mm, "holeDepth" : 100 * mm, "isTappedThrough" : true, "tappedDepth" : 12 * mm, "tapClearance" : 3, "locations" : qUnion([Q0, Q1]), "scope" : qUnion([Q2])});
        }
    });
